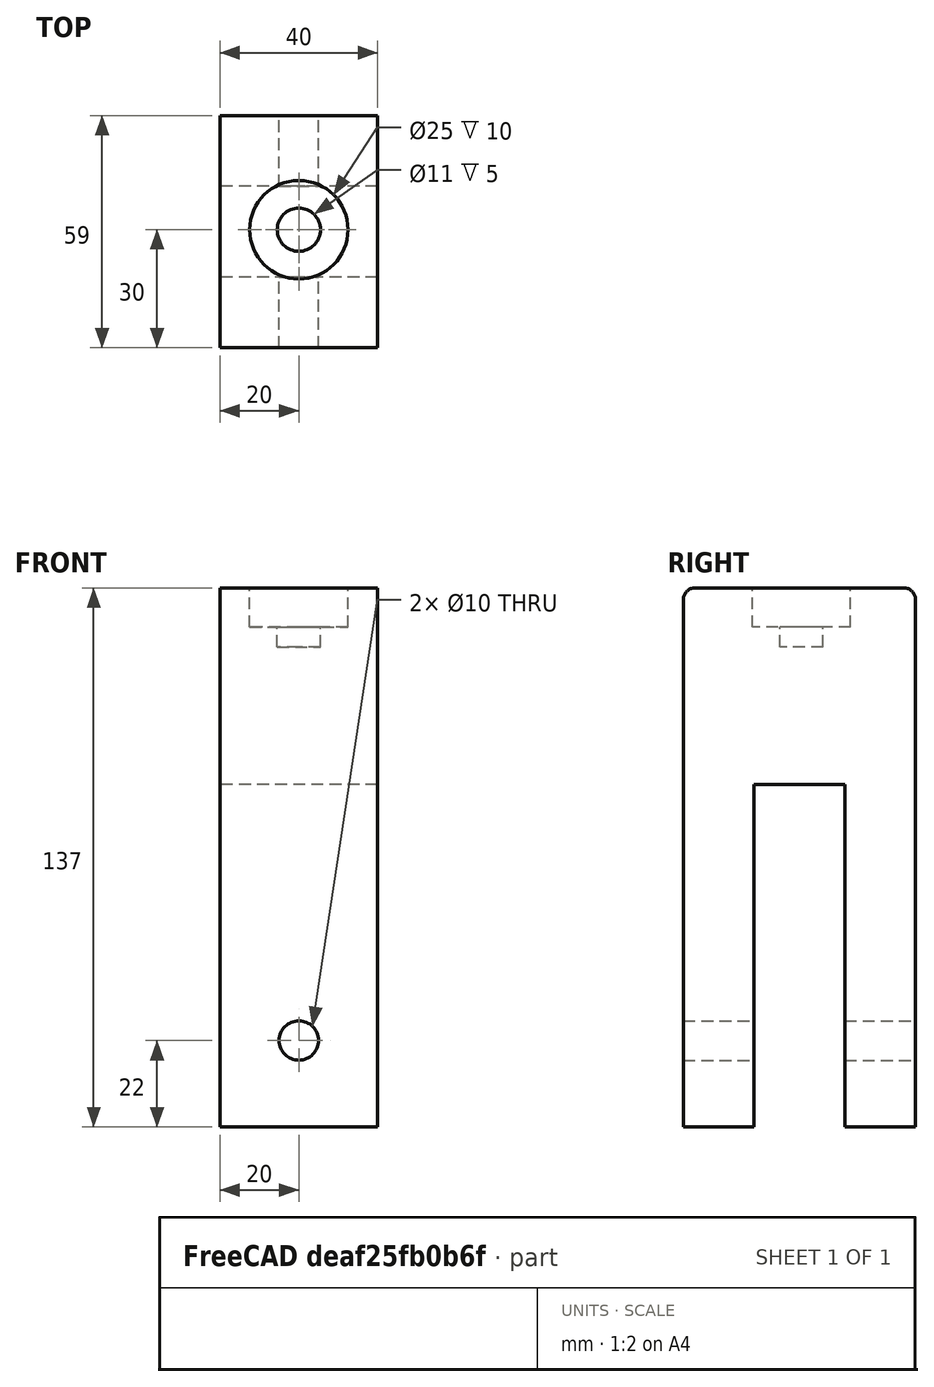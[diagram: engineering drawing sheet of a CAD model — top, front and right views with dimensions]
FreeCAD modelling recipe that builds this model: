
FCSTD DOCUMENT  (FreeCAD 0.16R6704 (Git))
Label: Object 6
License: All rights reserved
LicenseURL: http://en.wikipedia.org/wiki/All_rights_reserved
objects: Part::Cut×4, Part::Cylinder×3, Part::Box×2, Part::Fillet×1
note: 10 computed .brp shape members not serialized (recipe doc carries the construction recipe); baked Part::Feature solids carry a one-line shape summary decoded from their .brp

FEATURE [Part::Box] Box123  label="Cubo085"
  Height = 137
  Length = 59
  Placement = pos=(0,-5,0) rot=(0,0,1;0rad)
  Width = 40
FEATURE [Part::Box] Box124  label="Cubo086"
  Height = 87
  Length = 23
  Placement = pos=(18,-5,0) rot=(0,0,1;0rad)
  Width = 40
FEATURE [Part::Cut] Cut266
  Base = -> Box123
  Tool = -> Box124
FEATURE [Part::Cylinder] Cylinder242  label="Cilindro137"
  Angle = 360
  Height = 59
  Placement = pos=(0,15,22) rot=(0,1,0;1.5708rad)
  Radius = 5
FEATURE [Part::Cut] Cut267
  Base = -> Cut266
  Tool = -> Cylinder242
FEATURE [Part::Cylinder] Cylinder243  label="Cilindro138"
  Angle = 360
  Height = 10
  Placement = pos=(30,15,127) rot=(0,0,1;0rad)
  Radius = 12.5
FEATURE [Part::Cylinder] Cylinder244  label="Cilindro139"
  Angle = 360
  Height = 5
  Placement = pos=(30,15,122) rot=(0,0,1;0rad)
  Radius = 5.5
FEATURE [Part::Cut] Cut268
  Base = -> Cut267
  Tool = -> Cylinder243
FEATURE [Part::Cut] Cut269
  Base = -> Cut268
  Placement = pos=(-444,431,-153) rot=(0,0,1;1.5708rad)
  Tool = -> Cylinder244
FEATURE [Part::Fillet] Fillet
  Base = -> Cut269
  Edges = 2 edges r=3: [Edge2,Edge14]
